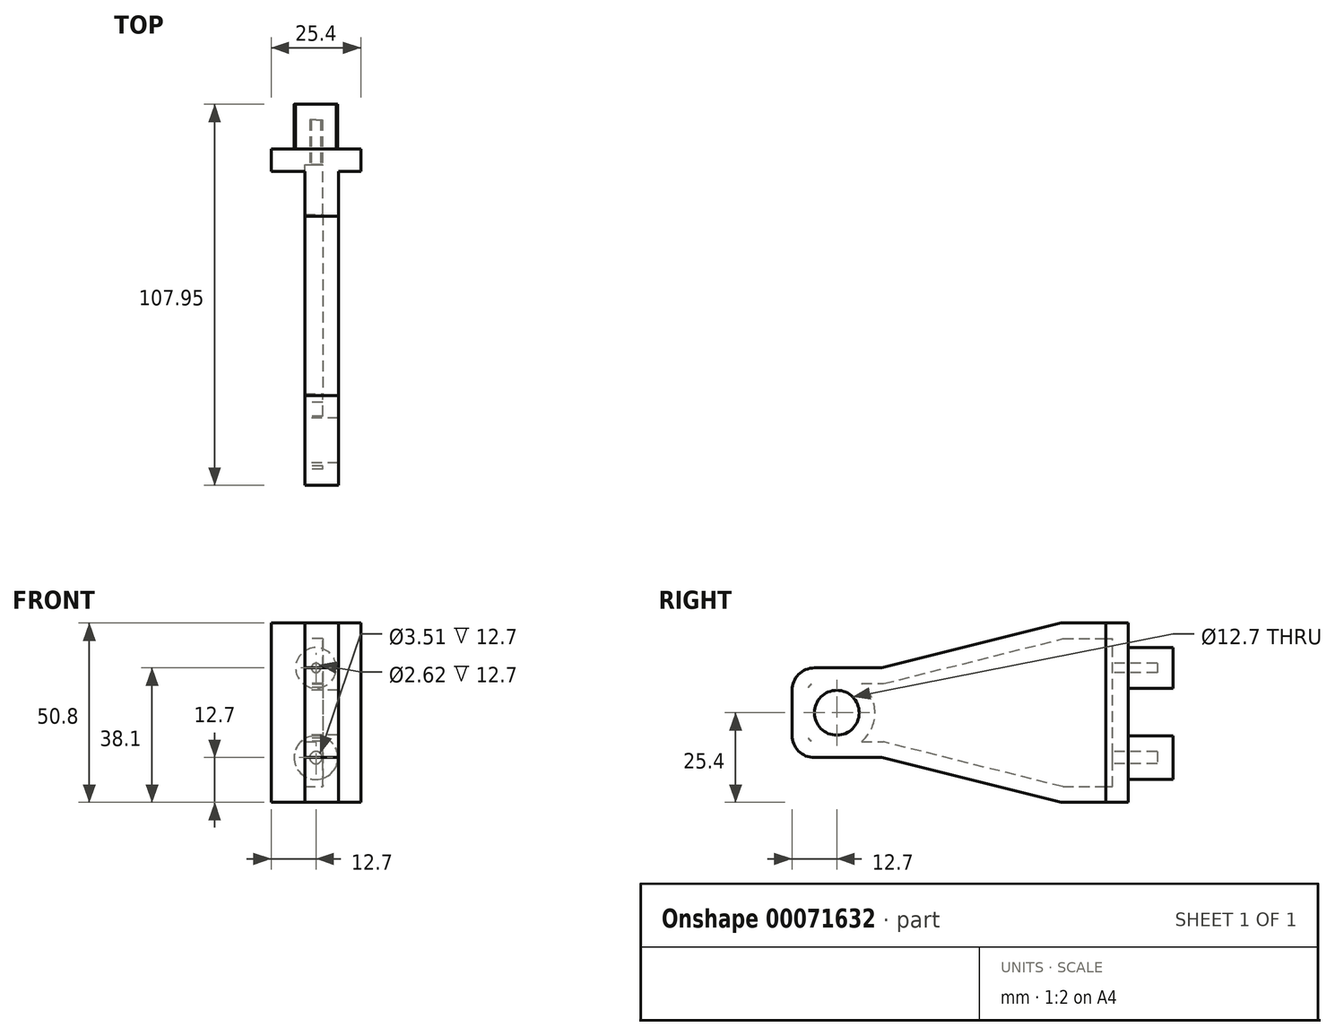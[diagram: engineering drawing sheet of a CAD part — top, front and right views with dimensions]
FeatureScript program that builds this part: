
annotation { "Feature Type Name" : "Feature", "Feature Type Description" : "" }
export const myFeature = defineFeature(function(context is Context, id is Id, definition is map)
    precondition{}
    {
        {
            var Q0;
            Q0=qCreatedBy(makeId("Front.planeOp"),FACE);
            var sketch = newSketch(context, id + "F0", { "sketchPlane" : qUnion([Q0])});
            skLineSegment(sketch, "E0.bottom", {"start": v(0, 0) * mm, "end": v(25.4, 0) * mm});
            skLineSegment(sketch, "E0.top", {"start": v(0, 50.8) * mm, "end": v(25.4, 50.8) * mm});
            skLineSegment(sketch, "E0.left", {"start": v(0, 0) * mm, "end": v(0, 50.8) * mm});
            skLineSegment(sketch, "E0.right", {"start": v(25.4, 0) * mm, "end": v(25.4, 50.8) * mm});
            skSolve(sketch);
        }
        {
            var Q0;
            Q0 = qSketchRegion(id + "F0", true);
            extrude(context, id + "F1", {"entities" : qUnion([Q0]), "depth" : 6.35 * mm});
        }
        {
            var Q0;
            Q0=makeQuery(id+"F1.opExtrude","CAP_FACE",FACE,{"disambiguationData":[OSD([sQuery(id+"F0.wireOp",EDGE,"E0.bottom"),sQuery(id+"F0.wireOp",EDGE,"E0.top"),sQuery(id+"F0.wireOp",EDGE,"E0.left"),sQuery(id+"F0.wireOp",EDGE,"E0.right")])],"isStart":false});
            var sketch = newSketch(context, id + "F2", { "sketchPlane" : qUnion([Q0])});
            skLineSegment(sketch, "E1.bottom", {"start": v(9.53, 0) * mm, "end": v(19.05, 0) * mm});
            skLineSegment(sketch, "E1.top", {"start": v(9.53, 50.8) * mm, "end": v(19.05, 50.8) * mm});
            skLineSegment(sketch, "E1.left", {"start": v(9.53, 0) * mm, "end": v(9.53, 50.8) * mm});
            skLineSegment(sketch, "E1.right", {"start": v(19.05, 0) * mm, "end": v(19.05, 50.8) * mm});
            skSolve(sketch);
        }
        {
            var Q0;
            Q0 = qSketchRegion(id + "F2", true);
            extrude(context, id + "F3", {"entities" : qUnion([Q0]), "operationType" : NewBodyOperationType.ADD, "depth" : 12.7 * mm});
        }
        {
            var Q0;
            Q0=makeQuery(id+"F3.opExtrude","CAP_FACE",FACE,{"disambiguationData":[OSD([sQuery(id+"F2.wireOp",EDGE,"E1.bottom"),sQuery(id+"F2.wireOp",EDGE,"E1.top"),sQuery(id+"F2.wireOp",EDGE,"E1.left"),sQuery(id+"F2.wireOp",EDGE,"E1.right")])],"isStart":false});
            cPlane(context, id + "F4", {"entities" : qUnion([Q0]), "cplaneType" : CPlaneType.OFFSET, "offset" : 50.8 * mm, "width" : 152.4 * mm, "height" : 152.4 * mm});
        }
        {
            var Q0;
            Q0=qCreatedBy(id+"F4.planeOp",FACE);
            var sketch = newSketch(context, id + "F5", { "sketchPlane" : qUnion([Q0])});
            skLineSegment(sketch, "E2.0", {"start": v(9.53, 12.7) * mm, "end": v(9.53, 38.1) * mm});
            skLineSegment(sketch, "E3.0", {"start": v(19.05, 12.7) * mm, "end": v(19.05, 38.1) * mm});
            skLineSegment(sketch, "E4", {"start": v(19.05, 38.1) * mm, "end": v(9.53, 38.1) * mm});
            skLineSegment(sketch, "E5", {"start": v(9.53, 12.7) * mm, "end": v(19.05, 12.7) * mm});
            skSolve(sketch);
        }
        {
            var Q1;
            Q1=makeQuery(id+"F3.opExtrude","CAP_FACE",FACE,{"disambiguationData":[OSD([sQuery(id+"F2.wireOp",EDGE,"E1.bottom"),sQuery(id+"F2.wireOp",EDGE,"E1.top"),sQuery(id+"F2.wireOp",EDGE,"E1.left"),sQuery(id+"F2.wireOp",EDGE,"E1.right")])],"isStart":false});
            var Q2;
            Q2=makeQuery(id+"F5.imprint","IMPRINT",FACE,{"disambiguationData":[TD([[makeQuery(id+"F5.imprint","IMPRINT",EDGE,{"derivedFrom":sQuery(id+"F5.wireOp",EDGE,"E2.0")}),-1.0]])]});
            loft(context, id + "F6", {"operationType" : NewBodyOperationType.ADD, "sheetProfilesArray" : [{ "sheetProfileEntities" : qUnion([Q1]) }, { "sheetProfileEntities" : qUnion([Q2]) }]});
        }
        {
            var Q0;
            Q0=makeQuery(id+"F6.opLoft","CAP_FACE",FACE,{"disambiguationData":[OSD([makeQuery(id+"F5.imprint","IMPRINT",FACE,{"disambiguationData":[TD([[makeQuery(id+"F5.imprint","IMPRINT",EDGE,{"derivedFrom":sQuery(id+"F5.wireOp",EDGE,"E2.0")}),-1.0]])]})])],"isStart":true});
            extrude(context, id + "F7", {"entities" : qUnion([Q0]), "operationType" : NewBodyOperationType.ADD, "depth" : 25.4 * mm});
        }
        {
            var Q0;
            Q0=makeQuery(id+"F7.opExtrude","CAP_EDGE",EDGE,{"disambiguationData":[OSD([sQuery(id+"F5.wireOp",EDGE,"E2.0"),sQuery(id+"F5.wireOp",EDGE,"E3.0"),sQuery(id+"F5.wireOp",EDGE,"E5")])],"isStart":false});
            var Q1;
            Q1=makeQuery(id+"F7.opExtrude","CAP_EDGE",EDGE,{"disambiguationData":[OSD([sQuery(id+"F5.wireOp",EDGE,"E2.0"),sQuery(id+"F5.wireOp",EDGE,"E3.0"),sQuery(id+"F5.wireOp",EDGE,"E4")])],"isStart":false});
            fillet(context, id + "F8", {"entities" : qUnion([Q0, Q1]), "radius" : 6.35 * mm, "tangentPropagation" : true, "allowEdgeOverflow" : false});
        }
        {
            var Q0;
            {var subQ0=sQuery(id+"F5.wireOp",EDGE,"E5");var subQ1=sQuery(id+"F5.wireOp",EDGE,"E4");var subQ2=sQuery(id+"F5.wireOp",EDGE,"E2.0");var subQ3=sQuery(id+"F2.wireOp",EDGE,"E1.left");Q0=makeQuery(id+"F7.boolean.opBoolean","MERGE",FACE,{"derivedFrom":[makeQuery(id+"F6.boolean.opBoolean","MERGE",FACE,{"derivedFrom":[makeQuery(id+"F3.opExtrude","SWEPT_FACE",FACE,{"disambiguationData":[OSD([subQ3])]}),makeQuery(id+"F6.opLoft","SWEPT_FACE",FACE,{"disambiguationData":[OSD([sQuery(id+"F0.wireOp",EDGE,"E0.bottom"),sQuery(id+"F0.wireOp",EDGE,"E0.top"),sQuery(id+"F2.wireOp",EDGE,"E1.bottom"),sQuery(id+"F2.wireOp",EDGE,"E1.top"),subQ3,subQ2,subQ1,subQ0])]})]}),makeQuery(id+"F7.opExtrude","SWEPT_FACE",FACE,{"disambiguationData":[OSD([subQ2,subQ1,subQ0])]})]});}
            var sketch = newSketch(context, id + "F9", { "sketchPlane" : qUnion([Q0])});
            skPoint(sketch, "E6", {"position": v(95.25, 25.4) * mm});
            skPoint(sketch, "E7", {"position": v(82.55, 25.4) * mm});
            skSolve(sketch);
        }
        {
            var Q0;
            Q0=sQuery(id+"F9.wireOp",VERTEX,"E7");
            var Q1;
            Q1=makeQuery(id+"F1.opExtrude","SWEPT_BODY",BODY,{"disambiguationData":[OSD([sQuery(id+"F0.wireOp",EDGE,"E0.bottom"),sQuery(id+"F0.wireOp",EDGE,"E0.top"),sQuery(id+"F0.wireOp",EDGE,"E0.left"),sQuery(id+"F0.wireOp",EDGE,"E0.right")])]});
            hole(context, id + "F10", {"style" : HoleStyle.SIMPLE, "endStyle" : HoleEndStyle.THROUGH, "holeDiameter" : 12.7 * mm, "locations" : qUnion([Q0]), "scope" : qUnion([Q1]), "isTappedThrough" : true});
        }
        {
            var Q0;
            Q0=makeQuery(id+"F1.opExtrude","CAP_FACE",FACE,{"disambiguationData":[OSD([sQuery(id+"F0.wireOp",EDGE,"E0.bottom"),sQuery(id+"F0.wireOp",EDGE,"E0.top"),sQuery(id+"F0.wireOp",EDGE,"E0.left"),sQuery(id+"F0.wireOp",EDGE,"E0.right")])],"isStart":true});
            var sketch = newSketch(context, id + "F11", { "sketchPlane" : qUnion([Q0])});
            skCircle(sketch, "E8", {"center": v(-12.7, 38.1) * mm, "radius": 5.76 * mm});
            skPoint(sketch, "E8.centerSnap0", {"position": v(-12.7, 50.8) * mm});
            skCircle(sketch, "E9", {"center": v(-12.7, 12.7) * mm, "radius": 6.2 * mm});
            skPoint(sketch, "E9.centerSnap0", {"position": v(-12.7, 0) * mm});
            skSolve(sketch);
        }
        {
            var Q0;
            Q0=makeQuery(id+"F11.imprint","IMPRINT",FACE,{"disambiguationData":[TD([[makeQuery(id+"F11.imprint","IMPRINT",EDGE,{"derivedFrom":sQuery(id+"F11.wireOp",EDGE,"E8")}),1.0]])]});
            var Q1;
            Q1=makeQuery(id+"F11.imprint","IMPRINT",FACE,{"disambiguationData":[TD([[makeQuery(id+"F11.imprint","IMPRINT",EDGE,{"derivedFrom":sQuery(id+"F11.wireOp",EDGE,"E9")}),1.0]])]});
            extrude(context, id + "F12", {"entities" : qUnion([Q0, Q1]), "operationType" : NewBodyOperationType.ADD, "depth" : 12.7 * mm});
        }
        {
            var Q0;
            {var subQ0=sQuery(id+"F5.wireOp",EDGE,"E5");var subQ1=sQuery(id+"F5.wireOp",EDGE,"E4");var subQ2=sQuery(id+"F5.wireOp",EDGE,"E2.0");var subQ3=sQuery(id+"F2.wireOp",EDGE,"E1.left");Q0=makeQuery(id+"F7.boolean.opBoolean","MERGE",FACE,{"derivedFrom":[makeQuery(id+"F6.boolean.opBoolean","MERGE",FACE,{"derivedFrom":[makeQuery(id+"F3.opExtrude","SWEPT_FACE",FACE,{"disambiguationData":[OSD([subQ3])]}),makeQuery(id+"F6.opLoft","SWEPT_FACE",FACE,{"disambiguationData":[OSD([sQuery(id+"F0.wireOp",EDGE,"E0.bottom"),sQuery(id+"F0.wireOp",EDGE,"E0.top"),sQuery(id+"F2.wireOp",EDGE,"E1.bottom"),sQuery(id+"F2.wireOp",EDGE,"E1.top"),subQ3,subQ2,subQ1,subQ0])]})]}),makeQuery(id+"F7.opExtrude","SWEPT_FACE",FACE,{"disambiguationData":[OSD([subQ2,subQ1,subQ0])]})]});}
            shell(context, id + "F13", {"entities" : qUnion([Q0]), "thickness" : 4.44 * mm});
        }
    });
